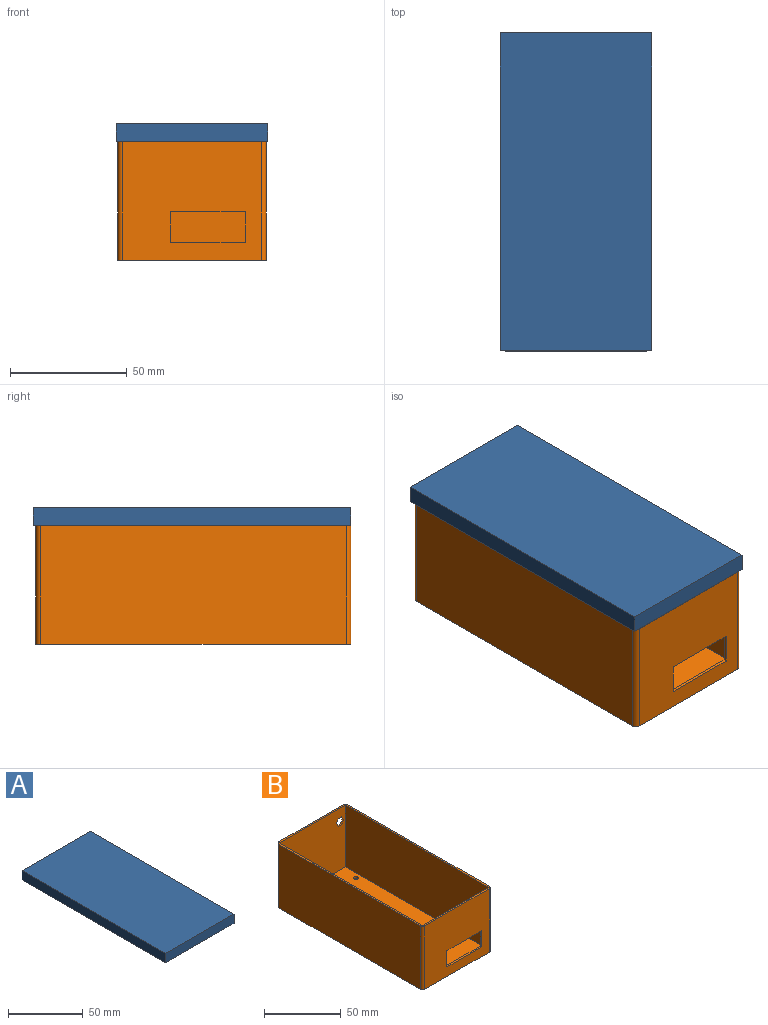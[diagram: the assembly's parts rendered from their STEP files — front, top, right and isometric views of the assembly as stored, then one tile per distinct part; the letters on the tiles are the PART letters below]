
ASSEMBLY  parts=2 mates=1
PART A: 11 faces, bbox 64.8x135.9x7.6 mm
  f0: plane 135.89x7.62mm, normal (-1,0,0), area 1035.5mm2, adj f1,f3,f4,f5
  f1: plane 64.77x7.62mm, normal (0,-1,0), area 493.5mm2, adj f0,f2,f4,f5
  f2: plane 135.89x7.62mm, normal (1,0,0), area 1035.5mm2, adj f1,f3,f4,f5
  f3: plane 64.77x7.62mm, normal (0,1,0), area 493.5mm2, adj f0,f2,f4,f5
  f4: plane 135.89x64.77mm, normal (0,0,1), area 8801.6mm2, adj f0,f1,f2,f3
  f5: plane 135.89x64.77mm, normal (0,0,-1), area 503.2mm2, adj f0,f1,f2,f3,f6,f7,f8,f9
  f6: plane 133.35x6.35mm, normal (1,0,0), area 846.8mm2, adj f5,f7,f9,f10
  f7: plane 62.23x6.35mm, normal (0,1,0), area 395.2mm2, adj f5,f6,f8,f10
  f8: plane 133.35x6.35mm, normal (-1,0,0), area 846.8mm2, adj f5,f7,f9,f10
  f9: plane 62.23x6.35mm, normal (0,-1,0), area 395.2mm2, adj f5,f6,f8,f10
  f10: plane 133.35x62.23mm, normal (0,0,-1), area 8298.4mm2, adj f6,f7,f8,f9
PART B: 35 faces, bbox 63.5x134.6x50.8 mm
  f0: plane 59.44x50.8mm, normal (0,1,0), area 2957mm2, adj f2,f4,f21,f22,f23,f24,f25,f26
  f1: plane 60.96x49.53mm, normal (0,-1,0), area 2957mm2, adj f2,f7,f8,f9,f23,f24,f25,f26
  f2: plane 134.62x63.5mm, normal (0,0,1), area 493.2mm2, adj f0,f1,f3,f5,f6,f7,f9,f10
  f3: plane 130.56x50.8mm, normal (-1,0,0), area 6632.2mm2, adj f2,f4,f19,f22
  f4: plane 134.62x63.5mm, normal (0,0,-1), area 8512.7mm2, adj f0,f3,f5,f6,f15,f16,f17,f18
  f5: plane 130.56x50.8mm, normal (1,0,0), area 6632.2mm2, adj f2,f4,f20,f21
  f6: plane 59.44x50.8mm, normal (0,-1,0), area 2603.3mm2, adj f2,f4,f11,f12,f13,f14,f19,f20
  f7: plane 132.08x49.53mm, normal (1,0,0), area 6541.9mm2, adj f1,f2,f8,f10
  f8: plane 132.08x60.96mm, normal (0,0,1), area 8019.4mm2, adj f1,f7,f9,f10,f15,f16,f17,f18
  f9: plane 132.08x49.53mm, normal (-1,0,0), area 6541.9mm2, adj f1,f2,f8,f10
  f10: plane 60.96x49.53mm, normal (0,1,0), area 2603.3mm2, adj f2,f7,f8,f9,f11,f12,f13,f14
  f11: plane 13x1.27mm, normal (-1,0,0), area 16.5mm2, adj f6,f10,f12,f14
  f12: plane 32x1.27mm, normal (0,0,-1), area 40.6mm2, adj f6,f10,f11,f13
  f13: plane 13x1.27mm, normal (1,0,0), area 16.5mm2, adj f6,f10,f12,f14
  f14: plane 32x1.27mm, normal (0,0,1), area 40.6mm2, adj f6,f10,f11,f13
  f15: cylinder r=1.6mm len=3.2mm, axis (0,0,1), area 12.8mm2, adj f4,f8
  f16: cylinder r=1.6mm len=3.2mm, axis (0,0,1), area 12.8mm2, adj f4,f8
  f17: cylinder r=1.6mm len=3.2mm, axis (0,0,1), area 12.8mm2, adj f4,f8
  f18: cylinder r=1.6mm len=3.2mm, axis (0,0,1), area 12.8mm2, adj f4,f8
  f19: cylinder r=2.03mm len=50.8mm, axis (0,0,1), area 162.1mm2, adj f2,f3,f4,f6
  f20: cylinder r=2.03mm len=50.8mm, axis (0,0,-1), area 162.1mm2, adj f2,f4,f5,f6
  f21: cylinder r=2.03mm len=50.8mm, axis (0,0,1), area 162.1mm2, adj f0,f2,f4,f5
  f22: cylinder r=2.03mm len=50.8mm, axis (0,0,-1), area 162.1mm2, adj f0,f2,f3,f4
  f23: plane 3.03x1.68mm, normal (0.87,0,0.49), area 4.4mm2, adj f0,f1,f24,f28
  f24: plane 2.97x1.78mm, normal (0.86,0,-0.51), area 4.4mm2, adj f0,f1,f23,f25
  f25: plane 3.46x1.27mm, normal (-0.02,0,-1), area 4.4mm2, adj f0,f1,f24,f26
  f26: plane 3.03x1.68mm, normal (-0.87,0,-0.49), area 4.4mm2, adj f0,f1,f25,f27
  f27: plane 2.97x1.78mm, normal (-0.86,0,0.51), area 4.4mm2, adj f0,f1,f26,f28
  f28: plane 3.46x1.27mm, normal (0.02,0,1), area 4.4mm2, adj f0,f1,f23,f27
  f29: plane 3.46x1.27mm, normal (-0.02,0,-1), area 4.4mm2, adj f0,f1,f30,f34
  f30: plane 3.03x1.68mm, normal (-0.87,0,-0.49), area 4.4mm2, adj f0,f1,f29,f31
  f31: plane 2.97x1.78mm, normal (-0.86,0,0.51), area 4.4mm2, adj f0,f1,f30,f32
  f32: plane 3.46x1.27mm, normal (0.02,0,1), area 4.4mm2, adj f0,f1,f31,f33
  f33: plane 3.03x1.68mm, normal (0.87,0,0.49), area 4.4mm2, adj f0,f1,f32,f34
  f34: plane 2.97x1.78mm, normal (0.86,0,-0.51), area 4.4mm2, adj f0,f1,f29,f33
PLACE A t=(-19.58,-90.23,10.83)mm
PLACE B t=(-19.58,-23.56,-14.57)mm fixed
MATE slider B.f2 <-> A.f5  axis (0,0,1) through (-50.06,-156.91,10.83)mm
